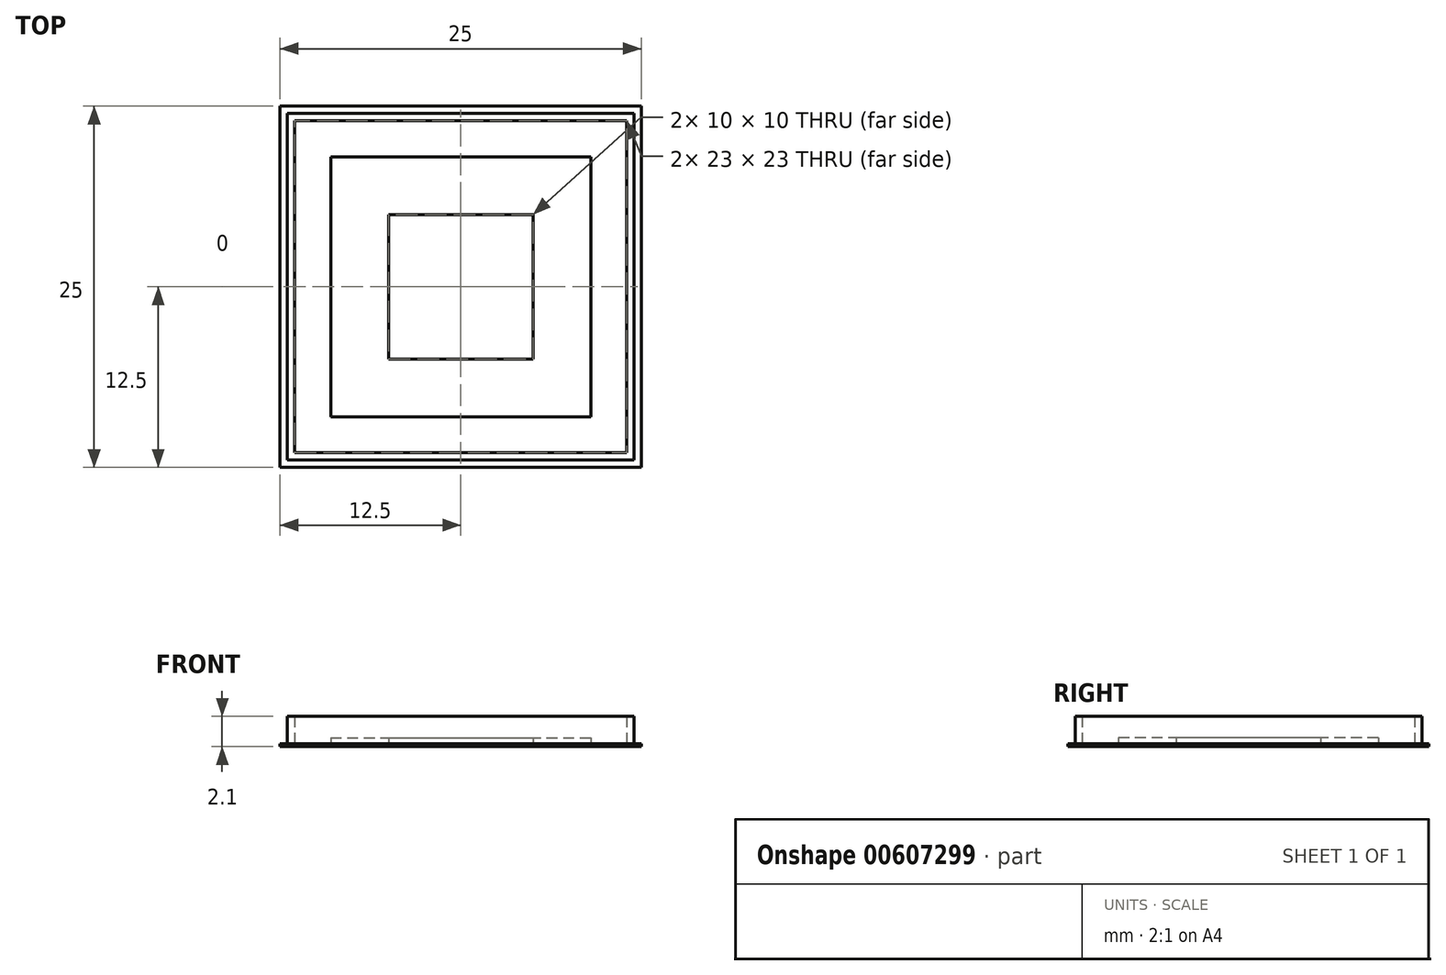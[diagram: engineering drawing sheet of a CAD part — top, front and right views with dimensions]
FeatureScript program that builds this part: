
annotation { "Feature Type Name" : "Feature", "Feature Type Description" : "" }
export const myFeature = defineFeature(function(context is Context, id is Id, definition is map)
    precondition{}
    {
        {
            var Q0;
            Q0=qCreatedBy(makeId("Top.planeOp"),FACE);
            var sketch = newSketch(context, id + "F0", { "sketchPlane" : qUnion([Q0])});
            skLineSegment(sketch, "E0.bottom", {"start": v(-9, 9) * mm, "end": v(9, 9) * mm});
            skLineSegment(sketch, "E0.top", {"start": v(-9, -9) * mm, "end": v(9, -9) * mm});
            skLineSegment(sketch, "E0.left", {"start": v(-9, 9) * mm, "end": v(-9, -9) * mm});
            skLineSegment(sketch, "E0.right", {"start": v(9, 9) * mm, "end": v(9, -9) * mm});
            skPoint(sketch, "E0.middle", {"position": v(0, 0) * mm});
            skLineSegment(sketch, "E1.bottom", {"start": v(-5, 5) * mm, "end": v(5, 5) * mm});
            skLineSegment(sketch, "E1.top", {"start": v(-5, -5) * mm, "end": v(5, -5) * mm});
            skLineSegment(sketch, "E1.left", {"start": v(-5, 5) * mm, "end": v(-5, -5) * mm});
            skLineSegment(sketch, "E1.right", {"start": v(5, 5) * mm, "end": v(5, -5) * mm});
            skSolve(sketch);
        }
        {
            var Q0;
            Q0 = qSketchRegion(id + "F0", true);
            extrude(context, id + "F1", {"entities" : qUnion([Q0]), "depth" : .5 * mm, "offsetDistance" : 25 * mm});
        }
        {
            var Q0;
            Q0=qCreatedBy(makeId("Top.planeOp"),FACE);
            var sketch = newSketch(context, id + "F2", { "sketchPlane" : qUnion([Q0])});
            skLineSegment(sketch, "E2.bottom", {"start": v(-11.5, 11.5) * mm, "end": v(11.5, 11.5) * mm});
            skLineSegment(sketch, "E2.top", {"start": v(-11.5, -11.5) * mm, "end": v(11.5, -11.5) * mm});
            skLineSegment(sketch, "E2.left", {"start": v(-11.5, 11.5) * mm, "end": v(-11.5, -11.5) * mm});
            skLineSegment(sketch, "E2.right", {"start": v(11.5, 11.5) * mm, "end": v(11.5, -11.5) * mm});
            skPoint(sketch, "E2.middle", {"position": v(0, 0) * mm});
            skLineSegment(sketch, "E3.bottom", {"start": v(-12.5, 12.5) * mm, "end": v(12.5, 12.5) * mm});
            skLineSegment(sketch, "E3.top", {"start": v(-12.5, -12.5) * mm, "end": v(12.5, -12.5) * mm});
            skLineSegment(sketch, "E3.left", {"start": v(-12.5, 12.5) * mm, "end": v(-12.5, -12.5) * mm});
            skLineSegment(sketch, "E3.right", {"start": v(12.5, 12.5) * mm, "end": v(12.5, -12.5) * mm});
            skSolve(sketch);
        }
        {
            var Q0;
            Q0 = qSketchRegion(id + "F2", true);
            extrude(context, id + "F3", {"entities" : qUnion([Q0]), "depth" : 0.1 * mm, "offsetDistance" : 25 * mm});
        }
        {
            var Q0;
            Q0=qCreatedBy(makeId("Top.planeOp"),FACE);
            var sketch = newSketch(context, id + "F4", { "sketchPlane" : qUnion([Q0])});
            skLineSegment(sketch, "E4.bottom", {"start": v(-5, 5) * mm, "end": v(5, 5) * mm});
            skLineSegment(sketch, "E4.top", {"start": v(-5, -5) * mm, "end": v(5, -5) * mm});
            skLineSegment(sketch, "E4.left", {"start": v(-5, 5) * mm, "end": v(-5, -5) * mm});
            skLineSegment(sketch, "E4.right", {"start": v(5, 5) * mm, "end": v(5, -5) * mm});
            skPoint(sketch, "E4.middle", {"position": v(0, 0) * mm});
            skLineSegment(sketch, "E5.bottom", {"start": v(-12.5, 12.5) * mm, "end": v(12.5, 12.5) * mm});
            skLineSegment(sketch, "E5.top", {"start": v(-12.5, -12.5) * mm, "end": v(12.5, -12.5) * mm});
            skLineSegment(sketch, "E5.left", {"start": v(-12.5, 12.5) * mm, "end": v(-12.5, -12.5) * mm});
            skLineSegment(sketch, "E5.right", {"start": v(12.5, 12.5) * mm, "end": v(12.5, -12.5) * mm});
            skSolve(sketch);
        }
        {
            var Q0;
            Q0 = qSketchRegion(id + "F4", true);
            extrude(context, id + "F5", {"entities" : qUnion([Q0]), "oppositeDirection" : true, "depth" : .1 * mm, "offsetDistance" : 25 * mm});
        }
        {
            var Q0;
            Q0=qCreatedBy(makeId("Top.planeOp"),FACE);
            var sketch = newSketch(context, id + "F6", { "sketchPlane" : qUnion([Q0])});
            skLineSegment(sketch, "E6.bottom", {"start": v(-11.5, 11.5) * mm, "end": v(11.5, 11.5) * mm});
            skLineSegment(sketch, "E6.top", {"start": v(-11.5, -11.5) * mm, "end": v(11.5, -11.5) * mm});
            skLineSegment(sketch, "E6.left", {"start": v(-11.5, 11.5) * mm, "end": v(-11.5, -11.5) * mm});
            skLineSegment(sketch, "E6.right", {"start": v(11.5, 11.5) * mm, "end": v(11.5, -11.5) * mm});
            skPoint(sketch, "E6.middle", {"position": v(0, 0) * mm});
            skLineSegment(sketch, "E7.bottom", {"start": v(-12, 12) * mm, "end": v(12, 12) * mm});
            skLineSegment(sketch, "E7.top", {"start": v(-12, -12) * mm, "end": v(12, -12) * mm});
            skLineSegment(sketch, "E7.left", {"start": v(-12, 12) * mm, "end": v(-12, -12) * mm});
            skLineSegment(sketch, "E7.right", {"start": v(12, 12) * mm, "end": v(12, -12) * mm});
            skSolve(sketch);
        }
        {
            var Q0;
            Q0 = qSketchRegion(id + "F6", true);
            extrude(context, id + "F7", {"entities" : qUnion([Q0]), "depth" : 2 * mm, "offsetDistance" : 25 * mm});
        }
    });
